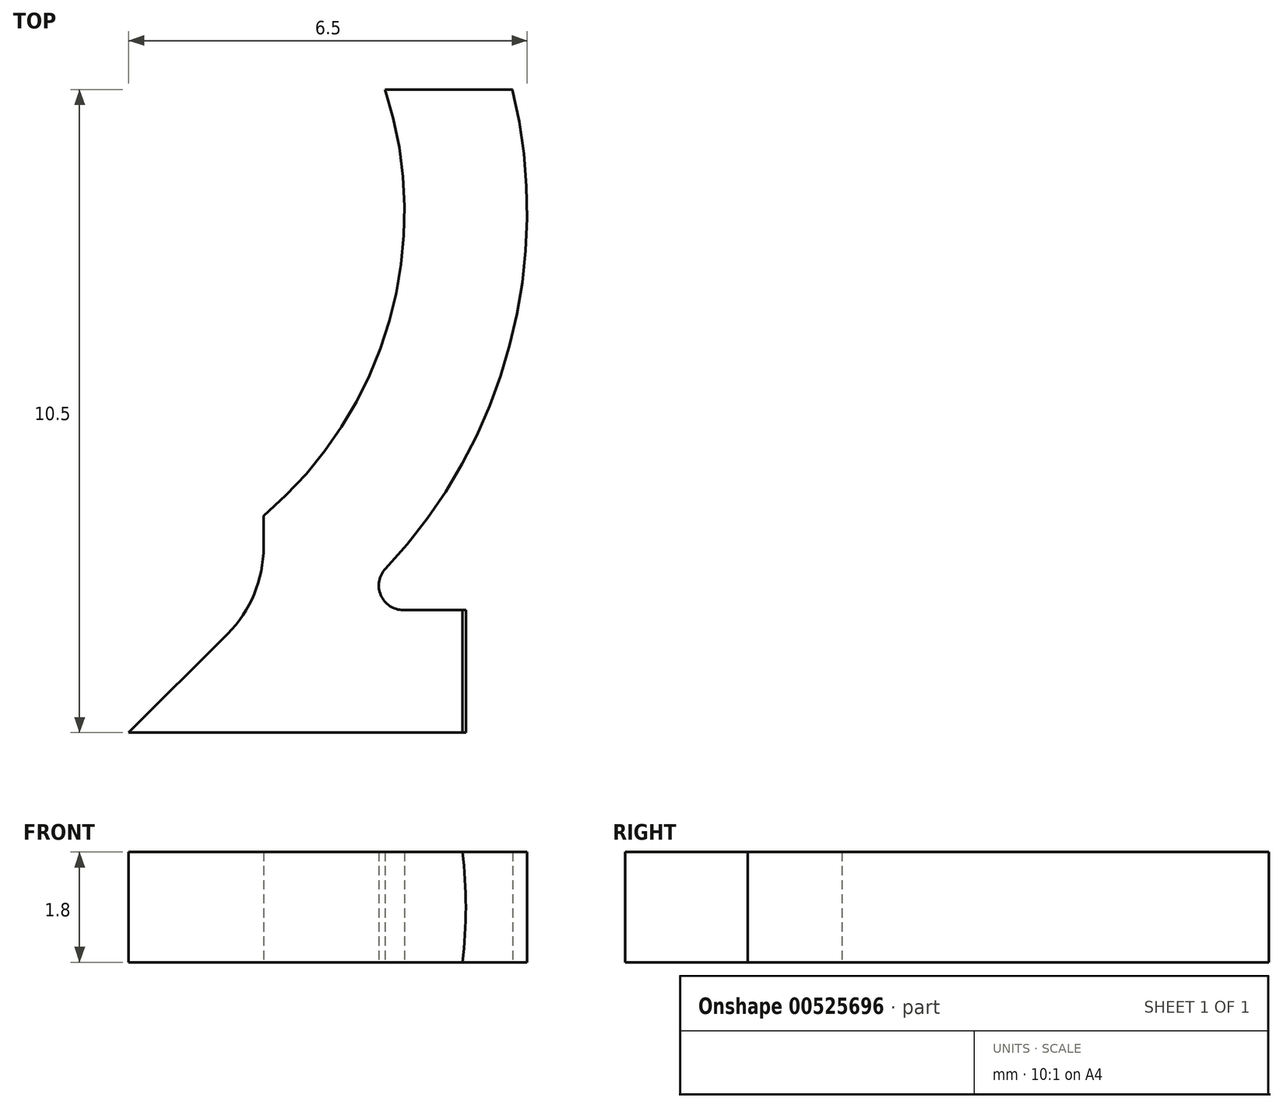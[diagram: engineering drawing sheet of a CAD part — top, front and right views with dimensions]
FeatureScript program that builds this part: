
annotation { "Feature Type Name" : "Feature", "Feature Type Description" : "" }
export const myFeature = defineFeature(function(context is Context, id is Id, definition is map)
    precondition{}
    {
        {
            var Q0;
            Q0=qCreatedBy(makeId("Top.planeOp"),FACE);
            var sketch = newSketch(context, id + "F0", { "sketchPlane" : qUnion([Q0])});
            skLineSegment(sketch, "E0", {"start": v(0, 0) * mm, "end": v(2, 0) * mm, "construction": true});
            skLineSegment(sketch, "E1", {"start": v(7.5, 0) * mm, "end": v(7.5, 2) * mm});
            skLineSegment(sketch, "E2", {"start": v(8.5, 8.5) * mm, "end": v(6.5, 8.5) * mm});
            skLineSegment(sketch, "E3", {"start": v(6.5, 8.5) * mm, "end": v(6.5, 8.5) * mm});
            skLineSegment(sketch, "E4", {"start": v(0, 2) * mm, "end": v(0, 2) * mm});
            skLineSegment(sketch, "E5", {"start": v(0, 2) * mm, "end": v(0, 0) * mm, "construction": true});
            skPoint(sketch, "E6.visualSharp", {"position": v(6.5, 2) * mm});
            skArc(sketch, "E6.filletArc", {"start": v(0, 2) * mm, "mid": v(1.01, 2.08) * mm, "end": v(2, 2.32) * mm, "construction": true});
            skArc(sketch, "E7.0", {"start": v(0, 0) * mm, "mid": v(2.92, 0.52) * mm, "end": v(5.48, 2) * mm, "construction": true});
            skLineSegment(sketch, "E8", {"start": v(0, 2) * mm, "end": v(5.48, 2) * mm, "construction": true});
            skLineSegment(sketch, "E9", {"start": v(6.48, 2) * mm, "end": v(7.5, 2) * mm});
            skArc(sketch, "E10", {"start": v(6.19, 2.67) * mm, "mid": v(8.22, 6.32) * mm, "end": v(8.26, 10.5) * mm});
            skLineSegment(sketch, "E11", {"start": v(2, 0) * mm, "end": v(2, 2.32) * mm, "construction": true});
            skArc(sketch, "E12", {"start": v(2, 2.32) * mm, "mid": v(3.16, 2.82) * mm, "end": v(4.2, 3.54) * mm, "construction": true});
            skLineSegment(sketch, "E13", {"start": v(2, 0) * mm, "end": v(7.5, 0) * mm});
            skLineSegment(sketch, "E14", {"start": v(6.18, 10.5) * mm, "end": v(8.26, 10.5) * mm});
            skLineSegment(sketch, "E15", {"start": v(2, 0) * mm, "end": v(3.61, 1.61) * mm});
            skLineSegment(sketch, "E16", {"start": v(4.2, 3.03) * mm, "end": v(4.2, 3.54) * mm});
            skPoint(sketch, "E17.visualSharp", {"position": v(4.2, 2.2) * mm});
            skArc(sketch, "E17.filletArc", {"start": v(3.61, 1.61) * mm, "mid": v(4.05, 2.26) * mm, "end": v(4.2, 3.03) * mm});
            skLineSegment(sketch, "E18", {"start": v(4.2, 3.54) * mm, "end": v(4.2, 3.54) * mm});
            skArc(sketch, "E19", {"start": v(4.2, 3.54) * mm, "mid": v(6.25, 6.72) * mm, "end": v(6.18, 10.5) * mm});
            skPoint(sketch, "E20.visualSharp", {"position": v(5.48, 2) * mm});
            skArc(sketch, "E20.filletArc", {"start": v(6.19, 2.67) * mm, "mid": v(6.11, 2.24) * mm, "end": v(6.48, 2) * mm});
            skSolve(sketch);
        }
        {
            var Q0;
            Q0 = qSketchRegion(id + "F0", true);
            extrude(context, id + "F1", {"entities" : qUnion([Q0]), "endBound" : BoundingType.SYMMETRIC, "depth" : 1.8 * mm, "offsetDistance" : 25 * mm});
        }
        {
            var Q0;
            Q0=makeQuery(id+"F1.opExtrude","SWEPT_FACE",FACE,{"disambiguationData":[OSD([sQuery(id+"F0.wireOp",EDGE,"E13")])]});
            var sketch = newSketch(context, id + "F2", { "sketchPlane" : qUnion([Q0])});
            skCircle(sketch, "E21", {"center": v(0, 0) * mm, "radius": 7.5 * mm});
            skCircle(sketch, "E22", {"center": v(0, 0) * mm, "radius": 8 * mm});
            skSolve(sketch);
        }
        {
            var Q0;
            Q0 = qSketchRegion(id + "F2", true);
            var Q1;
            Q1=makeQuery(id+"F1.opExtrude","SWEPT_FACE",FACE,{"disambiguationData":[OSD([sQuery(id+"F0.wireOp",EDGE,"E9")])]});
            extrude(context, id + "F3", {"entities" : qUnion([Q0]), "operationType" : NewBodyOperationType.REMOVE, "endBound" : BoundingType.UP_TO_SURFACE, "oppositeDirection" : true, "depth" : 25 * mm, "endBoundEntityFace" : qUnion([Q1]), "offsetDistance" : 25 * mm});
        }
    });
